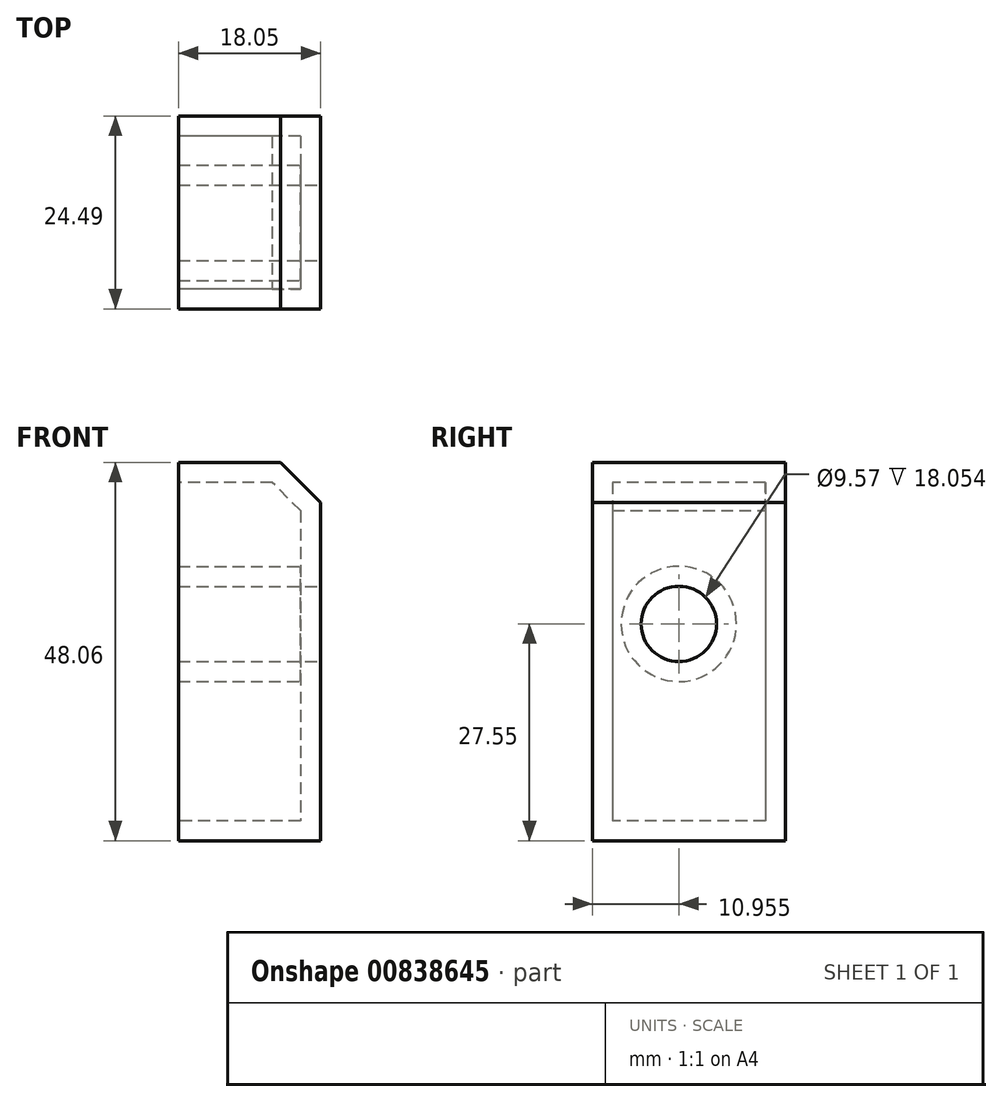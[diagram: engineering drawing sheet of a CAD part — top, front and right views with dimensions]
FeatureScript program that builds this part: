
annotation { "Feature Type Name" : "Feature", "Feature Type Description" : "" }
export const myFeature = defineFeature(function(context is Context, id is Id, definition is map)
    precondition{}
    {
        {
            var Q0;
            Q0=qCreatedBy(makeId("Top.planeOp"),FACE);
            var sketch = newSketch(context, id + "F0", { "sketchPlane" : qUnion([Q0])});
            skLineSegment(sketch, "E0.bottom", {"start": v(5.05, 41.05) * mm, "end": v(-13, 41.05) * mm});
            skLineSegment(sketch, "E0.top", {"start": v(5.05, 16.56) * mm, "end": v(-13, 16.56) * mm});
            skLineSegment(sketch, "E0.left", {"start": v(5.05, 41.05) * mm, "end": v(5.05, 16.56) * mm});
            skLineSegment(sketch, "E0.right", {"start": v(-13, 41.05) * mm, "end": v(-13, 16.56) * mm});
            skSolve(sketch);
        }
        {
            var Q0;
            Q0=makeQuery(id+"F0.imprint","IMPRINT",FACE,{"disambiguationData":[TD([[makeQuery(id+"F0.imprint","IMPRINT",EDGE,{"derivedFrom":sQuery(id+"F0.wireOp",EDGE,"E0.bottom")}),1.0]])]});
            extrude(context, id + "F1", {"entities" : qUnion([Q0]), "depth" : 48.06 * mm, "offsetDistance" : 25.4 * mm});
        }
        {
            var Q0;
            Q0=makeQuery(id+"F1.opExtrude","SWEPT_FACE",FACE,{"disambiguationData":[OSD([sQuery(id+"F0.wireOp",EDGE,"E0.left")])]});
            var sketch = newSketch(context, id + "F2", { "sketchPlane" : qUnion([Q0])});
            skCircle(sketch, "E1", {"center": v(27.51, 27.55) * mm, "radius": 4.79 * mm});
            skSolve(sketch);
        }
        {
            var Q0;
            Q0=makeQuery(id+"F2.imprint","IMPRINT",FACE,{"disambiguationData":[TD([[makeQuery(id+"F2.imprint","IMPRINT",EDGE,{"derivedFrom":sQuery(id+"F2.wireOp",EDGE,"E1")}),1.0]])]});
            extrude(context, id + "F3", {"entities" : qUnion([Q0]), "operationType" : NewBodyOperationType.REMOVE, "oppositeDirection" : true, "depth" : 59.62 * mm, "offsetDistance" : 25.4 * mm});
        }
        {
            var Q0;
            Q0=makeQuery(id+"F1.opExtrude","CAP_EDGE",EDGE,{"disambiguationData":[OSD([sQuery(id+"F0.wireOp",EDGE,"E0.left")])],"isStart":false});
            chamfer(context, id + "F4", {"entities" : qUnion([Q0]), "width" : 5.08 * mm, "tangentPropagation" : true});
        }
        {
            var Q0;
            Q0=makeQuery(id+"F1.opExtrude","SWEPT_FACE",FACE,{"disambiguationData":[OSD([sQuery(id+"F0.wireOp",EDGE,"E0.right")])]});
            shell(context, id + "F5", {"entities" : qUnion([Q0]), "thickness" : 2.54 * mm});
        }
    });
